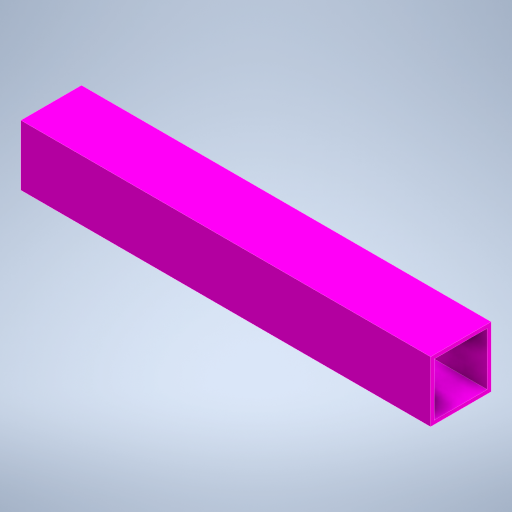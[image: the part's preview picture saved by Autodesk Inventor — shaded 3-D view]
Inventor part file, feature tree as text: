
AUTODESK INVENTOR PART (.ipt)
format: ipt  version: 2024 (Build 280153000, 153)  size: 218,112 bytes
history: native  units: in
note: dims shown in document units (in); Inventor stores cm internally (conversion verified against a paired STEP export)
features: extrude x1, sketch x1
ambient origin geometry x8: Origin, YZ Plane, XZ Plane, XY Plane, X Axis, Y Axis, Z Axis, Center Point
bodies: Solid1 (feature_tree)
feature tree (2):
  extrude  "Extrusion1"  Depth=1.0in
  sketch  "Sketch1"  dims[d0=1.0in d1=1.0in d2=0.0625in d3=6.765in d4=0.0in]
